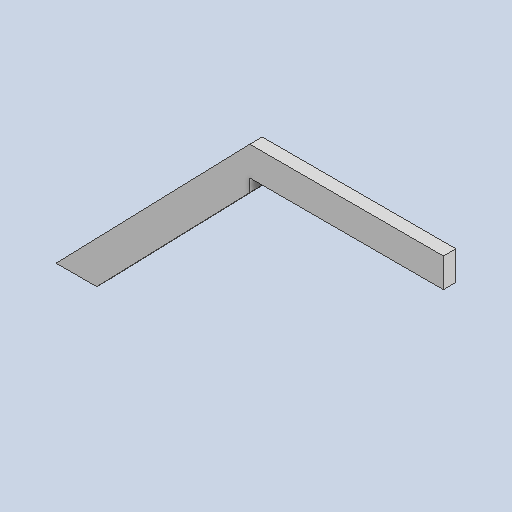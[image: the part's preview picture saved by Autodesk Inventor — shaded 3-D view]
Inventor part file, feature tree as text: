
AUTODESK INVENTOR PART (.ipt)
format: ipt  version: 2025 (Build 290162000, 162)  size: 85,504 bytes
history: native  units: in
note: dims shown in document units (in); Inventor stores cm internally (conversion verified against a paired STEP export)
features: other x3, sketch x1
ambient origin geometry x8: Origin, YZ Plane, XZ Plane, XY Plane, X Axis, Y Axis, Z Axis, Center Point
bodies: Solid1 (feature_tree)
feature tree (4):
  other  "side-side1.ipt"
  other  "Solid1::side-side1.ipt"
  other  "TaggingFeature1"
  sketch  "Sketch1"  dims[d0=0.3937in]
